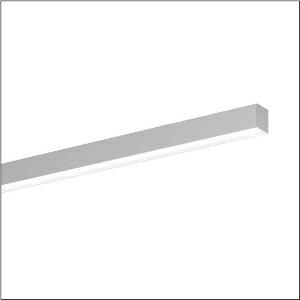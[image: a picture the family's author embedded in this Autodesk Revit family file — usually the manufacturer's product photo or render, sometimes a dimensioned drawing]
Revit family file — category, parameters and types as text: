
# Revit family: silica_r__21_51mx23dc3asb_5b95
name_source: partatom
category: Lighting Fixtures
units: mm (PartAtom-declared; Revit-internal decimal feet)

## family parameters
Cut with Voids When Loaded = No
Host = Face
Light Source = No
Part Type = Normal
Room Calculation Point = No
Round Connector Dimension = Use Diameter
Shared = No

## types (1)
- --- (1 x LED, 8200 lm, 62.2 W, 3000K)
    Apparent Load = 62 VA
    CIE Flux Codes = 78 96 99 100 100
    Color Rendering = 80
    Color Temperature = 3000K
    Default Elevation = 1800 mm
    Description = Silica® 21, office luminaire, primary optical cover: prismatic diffuser, of PMMA, CAT 2 (L<= 3000cd/m²), light emission: direct distribution, primary light characteristic: symmetric, installation type: surface-mounted, LED, rated luminous flux: 8.200lm, luminous efficacy: 132lm/W, light colour: 830, colour temperature: 3000K, with terminal, 3+2-pole, max. 2.5mm², mains connection: 220..240V, AC, 50/60Hz, rated input power: 62.2W, luminaire housing, of aluminium, metallic grey (RAL 9006), length: 3.004mm, width: 53mm, height: 53mm, protection rating (complete): IP20, insulation class (complete): insulation class I (protective earthing), certification: CE, permissible operating ambient temperature: 0..+35°C, standard: EN 50419, packaging unit: 1 piece
    Height = 0 mm  [stored 0 ft]
    Lamp = 1 x LED
    Lamp Light Flux = 8200 lm
    Lamp Power = 62.2 W
    Lamp count = 1
    Length = 3004 mm
    Luminous efficacy = 132 lm/W
    Manufacturer = Siteco
    ModVariant = No
    Model = 51MX23DC3ASB
    Mounting Place = Ceiling
    Mounting Type = Recessed
    Number of Poles = 1
    OnlyDefault = Yes
    Power Factor = 1
    Product Name = Silica® 21
    Product group = office luminaire | ceiling recessed
    ProductGroupID = 401
    Protection Class = Protection class I
    Protection Degree = IP 20
    RLX_Detail_Level = 1
    RLX_Emergency_Light_Flux = 0 lm
    RLX_Emergency_Type = 0
    RLX_Emergency_Type_DB = No
    RlxData = <blob elided: 21241 chars, md5=e8afd606>
    Socket = socket
    Standby Power = 0 W
    System Light Flux = 8200 lm
    System Power = 62 W
    Type Comments = factory setting: luminous flux: 100 % | dim-lin: 254 | 345 mA
    Type Image = l_1313588.jpg
    URL = http://relux.com
    VarID = @adj_067729
    Voltage = 0 V
    Weight = 0.00 kg
    Width = 53 mm

note: [stored X ft] marks values corroborated as IEEE doubles in the binary element streams (Revit-internal decimal feet)

## geometry (parser evidence)
native form markers: Blend x4, Sweep x10
no freeform markers — native parametric forms only
